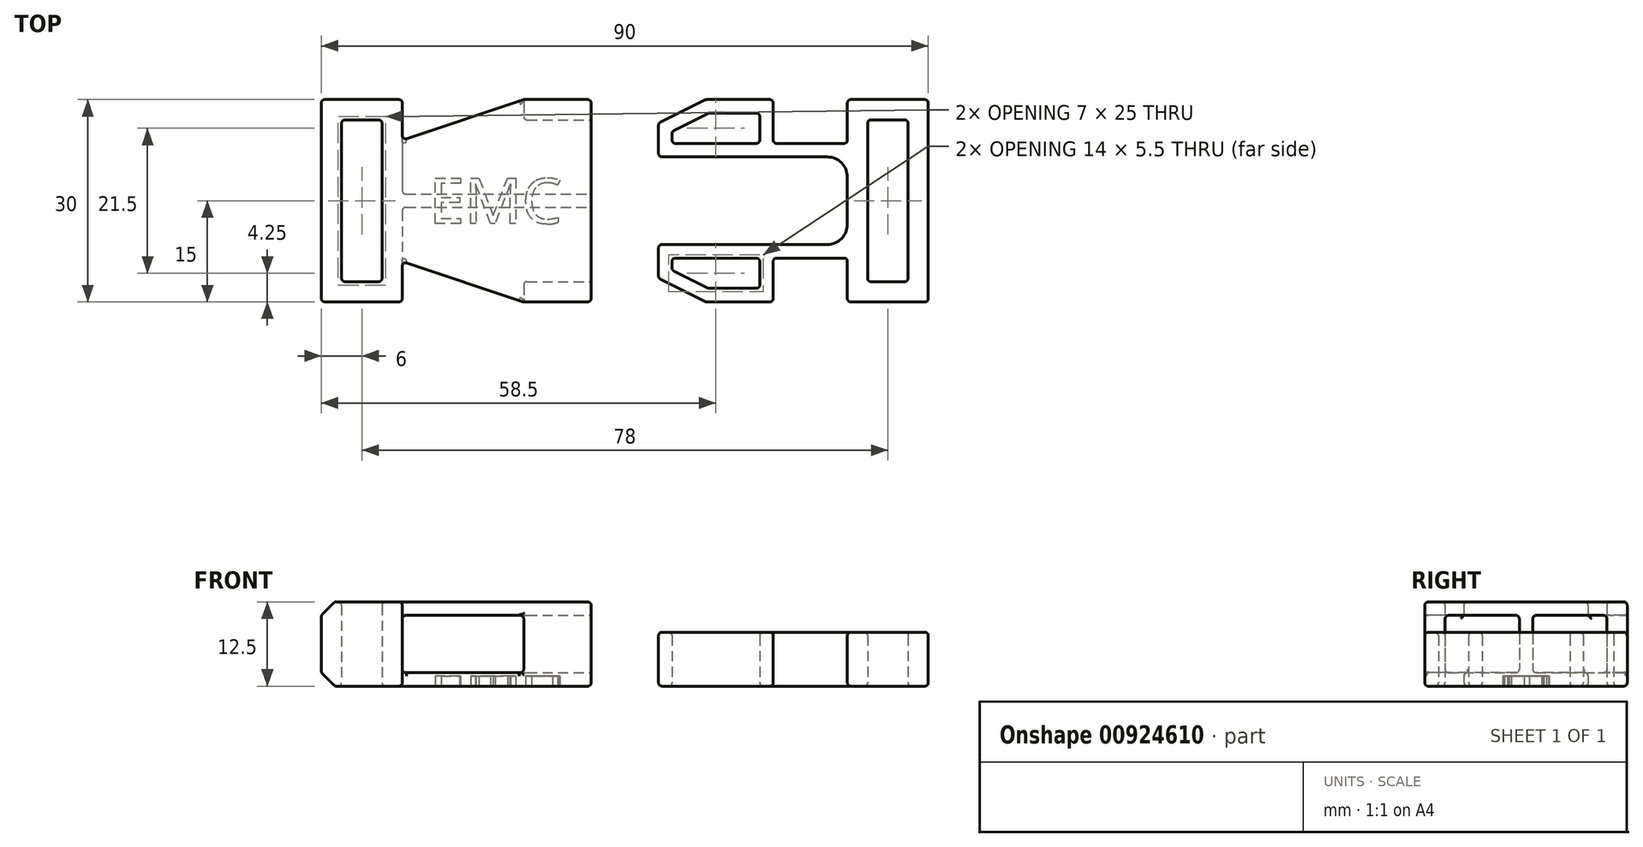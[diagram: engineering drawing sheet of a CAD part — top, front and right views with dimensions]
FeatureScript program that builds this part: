
annotation { "Feature Type Name" : "Feature", "Feature Type Description" : "" }
export const myFeature = defineFeature(function(context is Context, id is Id, definition is map)
    precondition{}
    {
        {
            var Q0;
            Q0=qCreatedBy(makeId("Top.planeOp"),FACE);
            var sketch = newSketch(context, id + "F0", { "sketchPlane" : qUnion([Q0])});
            skLineSegment(sketch, "E0.bottom", {"start": v(-10, 0) * mm, "end": v(-50, 0) * mm, "construction": true});
            skLineSegment(sketch, "E0.top", {"start": v(-10, 30) * mm, "end": v(-50, 30) * mm, "construction": true});
            skLineSegment(sketch, "E0.left", {"start": v(-10, 0) * mm, "end": v(-10, 30) * mm, "construction": true});
            skLineSegment(sketch, "E0.right", {"start": v(-50, 0) * mm, "end": v(-50, 30) * mm, "construction": true});
            skLineSegment(sketch, "E1", {"start": v(-10, 0) * mm, "end": v(-10, 30) * mm});
            skLineSegment(sketch, "E2", {"start": v(-10, 30) * mm, "end": v(-20, 30) * mm});
            skLineSegment(sketch, "E3", {"start": v(-20, 30) * mm, "end": v(-20, 24) * mm});
            skLineSegment(sketch, "E4", {"start": v(-20, 24) * mm, "end": v(-38, 24) * mm});
            skLineSegment(sketch, "E5", {"start": v(-38, 24) * mm, "end": v(-38, 30) * mm});
            skLineSegment(sketch, "E6", {"start": v(-38, 30) * mm, "end": v(-50, 30) * mm});
            skLineSegment(sketch, "E7", {"start": v(-50, 30) * mm, "end": v(-50, 0) * mm});
            skLineSegment(sketch, "E8", {"start": v(-50, 0) * mm, "end": v(-38, 0) * mm});
            skLineSegment(sketch, "E9", {"start": v(-38, 0) * mm, "end": v(-38, 6) * mm});
            skLineSegment(sketch, "E10", {"start": v(-38, 6) * mm, "end": v(-20, 6) * mm});
            skLineSegment(sketch, "E11", {"start": v(-20, 6) * mm, "end": v(-20, 0) * mm});
            skLineSegment(sketch, "E12", {"start": v(-20, 0) * mm, "end": v(-10, 0) * mm});
            skLineSegment(sketch, "E13.bottom", {"start": v(-47, 27) * mm, "end": v(-41, 27) * mm});
            skLineSegment(sketch, "E13.top", {"start": v(-47, 3) * mm, "end": v(-41, 3) * mm});
            skLineSegment(sketch, "E13.left", {"start": v(-47, 27) * mm, "end": v(-47, 3) * mm});
            skLineSegment(sketch, "E13.right", {"start": v(-41, 27) * mm, "end": v(-41, 3) * mm});
            skLineSegment(sketch, "E14.bottom", {"start": v(-38, 16) * mm, "end": v(-10, 16) * mm});
            skLineSegment(sketch, "E14.top", {"start": v(-38, 14) * mm, "end": v(-10, 14) * mm});
            skLineSegment(sketch, "E14.left", {"start": v(-41, 16) * mm, "end": v(-41, 14) * mm});
            skLineSegment(sketch, "E14.right", {"start": v(-10, 16) * mm, "end": v(-10, 14) * mm});
            skLineSegment(sketch, "E15", {"start": v(-20, 27) * mm, "end": v(-10, 27) * mm});
            skLineSegment(sketch, "E16", {"start": v(-20, 3) * mm, "end": v(-10, 3) * mm});
            skLineSegment(sketch, "E17", {"start": v(-50, 15) * mm, "end": v(-10, 15) * mm, "construction": true});
            skLineSegment(sketch, "E18", {"start": v(-10, 30) * mm, "end": v(0, 30) * mm, "construction": true});
            skLineSegment(sketch, "E19", {"start": v(-20, 24) * mm, "end": v(0, 24) * mm, "construction": true});
            skLineSegment(sketch, "E20", {"start": v(-10, 16) * mm, "end": v(0, 16) * mm, "construction": true});
            skLineSegment(sketch, "E21", {"start": v(-10, 15) * mm, "end": v(0, 15) * mm, "construction": true});
            skLineSegment(sketch, "E22", {"start": v(0, 21.5) * mm, "end": v(0, 26.5) * mm});
            skLineSegment(sketch, "E23", {"start": v(0, 26.5) * mm, "end": v(7, 30) * mm});
            skLineSegment(sketch, "E24", {"start": v(7, 30) * mm, "end": v(17, 30) * mm});
            skLineSegment(sketch, "E25", {"start": v(17, 30) * mm, "end": v(17, 23.5) * mm});
            skLineSegment(sketch, "E26", {"start": v(17, 23.5) * mm, "end": v(28, 23.5) * mm});
            skLineSegment(sketch, "E27", {"start": v(28, 23.5) * mm, "end": v(28, 30) * mm});
            skLineSegment(sketch, "E28", {"start": v(28, 30) * mm, "end": v(40, 30) * mm});
            skLineSegment(sketch, "E29", {"start": v(40, 30) * mm, "end": v(40, 15) * mm});
            skLineSegment(sketch, "E30", {"start": v(28, 15) * mm, "end": v(28, 18.5) * mm});
            skLineSegment(sketch, "E31", {"start": v(25, 21.5) * mm, "end": v(0, 21.5) * mm});
            skLineSegment(sketch, "E32.MirrorCS", {"start": v(25, 8.5) * mm, "end": v(0, 8.5) * mm});
            skLineSegment(sketch, "E33.MirrorCS", {"start": v(28, 15) * mm, "end": v(28, 11.5) * mm});
            skLineSegment(sketch, "E34.MirrorCS", {"start": v(40, 0) * mm, "end": v(40, 15) * mm});
            skLineSegment(sketch, "E35.MirrorCS", {"start": v(28, 0) * mm, "end": v(40, 0) * mm});
            skLineSegment(sketch, "E36.MirrorCS", {"start": v(28, 6.5) * mm, "end": v(28, 0) * mm});
            skLineSegment(sketch, "E37.MirrorCS", {"start": v(17, 6.5) * mm, "end": v(28, 6.5) * mm});
            skLineSegment(sketch, "E38.MirrorCS", {"start": v(17, 0) * mm, "end": v(17, 6.5) * mm});
            skLineSegment(sketch, "E39.MirrorCS", {"start": v(7, 0) * mm, "end": v(17, 0) * mm});
            skLineSegment(sketch, "E40.MirrorCS", {"start": v(0, 3.5) * mm, "end": v(7, 0) * mm});
            skLineSegment(sketch, "E41.MirrorCS", {"start": v(0, 8.5) * mm, "end": v(0, 3.5) * mm});
            skPoint(sketch, "E42.visualSharp", {"position": v(28, 21.5) * mm});
            skArc(sketch, "E42.filletArc", {"start": v(28, 18.5) * mm, "mid": v(27.12, 20.62) * mm, "end": v(25, 21.5) * mm});
            skPoint(sketch, "E43.visualSharp", {"position": v(28, 8.5) * mm});
            skArc(sketch, "E43.filletArc", {"start": v(25, 8.5) * mm, "mid": v(27.12, 9.38) * mm, "end": v(28, 11.5) * mm});
            skLineSegment(sketch, "E44.bottom", {"start": v(31, 27) * mm, "end": v(37, 27) * mm});
            skLineSegment(sketch, "E44.top", {"start": v(31, 3) * mm, "end": v(37, 3) * mm});
            skLineSegment(sketch, "E44.left", {"start": v(31, 27) * mm, "end": v(31, 3) * mm});
            skLineSegment(sketch, "E44.right", {"start": v(37, 27) * mm, "end": v(37, 3) * mm});
            skLineSegment(sketch, "E45.0", {"start": v(15, 28) * mm, "end": v(15, 23.5) * mm});
            skLineSegment(sketch, "E45.1", {"start": v(7.47, 28) * mm, "end": v(15, 28) * mm});
            skLineSegment(sketch, "E45.2", {"start": v(2, 25.26) * mm, "end": v(7.47, 28) * mm});
            skLineSegment(sketch, "E45.3", {"start": v(2, 23.5) * mm, "end": v(2, 25.26) * mm});
            skLineSegment(sketch, "E46", {"start": v(2, 23.5) * mm, "end": v(15, 23.5) * mm});
            skLineSegment(sketch, "E47.MirrorCS", {"start": v(2, 6.5) * mm, "end": v(15, 6.5) * mm});
            skLineSegment(sketch, "E48.MirrorCS", {"start": v(2, 6.5) * mm, "end": v(2, 4.74) * mm});
            skLineSegment(sketch, "E49.MirrorCS", {"start": v(2, 4.74) * mm, "end": v(7.47, 2) * mm});
            skLineSegment(sketch, "E50.MirrorCS", {"start": v(7.47, 2) * mm, "end": v(15, 2) * mm});
            skLineSegment(sketch, "E51.MirrorCS", {"start": v(15, 2) * mm, "end": v(15, 6.5) * mm});
            skLineSegment(sketch, "E52", {"start": v(-38, 24) * mm, "end": v(-38, 6) * mm});
            skLineSegment(sketch, "E53", {"start": v(-38, 6) * mm, "end": v(-20, 0) * mm});
            skLineSegment(sketch, "E54", {"start": v(-38, 24) * mm, "end": v(-20, 30) * mm});
            skSolve(sketch);
        }
        {
            var Q0;
            Q0=makeQuery(id+"F0.imprint","IMPRINT",FACE,{"disambiguationData":[TD([[makeQuery(id+"F0.imprint","IMPRINT",EDGE,{"derivedFrom":sQuery(id+"F0.wireOp",EDGE,"E22")}),-1.0]])]});
            extrude(context, id + "F1", {"entities" : qUnion([Q0]), "depth" : 8 * mm, "offsetDistance" : 25 * mm});
        }
        {
            var Q0;
            {var subQ1=sQuery(id+"F0.wireOp",EDGE,"E4");Q0=makeQuery(id+"F0.imprint","IMPRINT",FACE,{"disambiguationData":[TD([[makeQuery(id+"F0.imprint","IMPRINT",EDGE,{"derivedFrom":subQ1}),1.0]])]});}
            var Q1;
            {var subQ1=sQuery(id+"F0.wireOp",EDGE,"E10");Q1=makeQuery(id+"F0.imprint","IMPRINT",FACE,{"disambiguationData":[TD([[makeQuery(id+"F0.imprint","IMPRINT",EDGE,{"derivedFrom":subQ1}),1.0]])]});}
            var Q2;
            {var subQ0=sQuery(id+"F0.wireOp",EDGE,"E12");Q2=makeQuery(id+"F0.imprint","IMPRINT",FACE,{"disambiguationData":[TD([[makeQuery(id+"F0.imprint","IMPRINT",EDGE,{"derivedFrom":subQ0}),1.0]])]});}
            var Q3;
            {var subQ2=sQuery(id+"F0.wireOp",EDGE,"E5");Q3=makeQuery(id+"F0.imprint","IMPRINT",FACE,{"disambiguationData":[TD([[makeQuery(id+"F0.imprint","IMPRINT",EDGE,{"derivedFrom":subQ2}),1.0]])]});}
            var Q4;
            {var subQ0=sQuery(id+"F0.wireOp",EDGE,"E2");Q4=makeQuery(id+"F0.imprint","IMPRINT",FACE,{"disambiguationData":[TD([[makeQuery(id+"F0.imprint","IMPRINT",EDGE,{"derivedFrom":subQ0}),1.0]])]});}
            var Q5;
            {var subQ0=sQuery(id+"F0.wireOp",EDGE,"E14.bottom");Q5=makeQuery(id+"F0.imprint","IMPRINT",FACE,{"disambiguationData":[TD([[makeQuery(id+"F0.imprint","IMPRINT",EDGE,{"derivedFrom":subQ0}),-1.0]])]});}
            var Q6;
            {var subQ0=sQuery(id+"F0.wireOp",EDGE,"E10");Q6=makeQuery(id+"F0.imprint","IMPRINT",FACE,{"disambiguationData":[TD([[makeQuery(id+"F0.imprint","IMPRINT",EDGE,{"derivedFrom":subQ0}),-1.0]])]});}
            var Q7;
            {var subQ2=sQuery(id+"F0.wireOp",EDGE,"E4");Q7=makeQuery(id+"F0.imprint","IMPRINT",FACE,{"disambiguationData":[TD([[makeQuery(id+"F0.imprint","IMPRINT",EDGE,{"derivedFrom":subQ2}),-1.0]])]});}
            extrude(context, id + "F2", {"entities" : qUnion([Q0, Q1, Q2, Q3, Q4, Q5, Q6, Q7]), "depth" : (8.5 + 4) * mm, "offsetDistance" : 25 * mm});
        }
        {
            var Q0;
            {var subQ1=sQuery(id+"F0.wireOp",EDGE,"E10");Q0=makeQuery(id+"F0.imprint","IMPRINT",FACE,{"disambiguationData":[TD([[makeQuery(id+"F0.imprint","IMPRINT",EDGE,{"derivedFrom":subQ1}),1.0]])]});}
            var Q1;
            {var subQ1=sQuery(id+"F0.wireOp",EDGE,"E4");Q1=makeQuery(id+"F0.imprint","IMPRINT",FACE,{"disambiguationData":[TD([[makeQuery(id+"F0.imprint","IMPRINT",EDGE,{"derivedFrom":subQ1}),1.0]])]});}
            var Q2;
            {var subQ0=sQuery(id+"F0.wireOp",EDGE,"E10");Q2=makeQuery(id+"F0.imprint","IMPRINT",FACE,{"disambiguationData":[TD([[makeQuery(id+"F0.imprint","IMPRINT",EDGE,{"derivedFrom":subQ0}),-1.0]])]});}
            var Q3;
            {var subQ2=sQuery(id+"F0.wireOp",EDGE,"E4");Q3=makeQuery(id+"F0.imprint","IMPRINT",FACE,{"disambiguationData":[TD([[makeQuery(id+"F0.imprint","IMPRINT",EDGE,{"derivedFrom":subQ2}),-1.0]])]});}
            extrude(context, id + "F3", {"entities" : qUnion([Q0, Q1, Q2, Q3]), "operationType" : NewBodyOperationType.REMOVE, "depth" : (8.5 + 2) * mm, "offsetDistance" : 25 * mm, "hasSecondDirection" : true, "secondDirectionOppositeDirection" : false, "secondDirectionDepth" : 2 * mm});
        }
        {
            var Q0;
            Q0=makeQuery(id+"F2.opExtrude","CAP_EDGE",EDGE,{"disambiguationData":[OSD([sQuery(id+"F0.wireOp",EDGE,"E7")])],"isStart":false});
            var Q1;
            Q1=makeQuery(id+"F2.opExtrude","CAP_EDGE",EDGE,{"disambiguationData":[OSD([sQuery(id+"F0.wireOp",EDGE,"E7")])],"isStart":true});
            chamfer(context, id + "F4", {"entities" : qUnion([Q0, Q1]), "width" : 2 * mm, "tangentPropagation" : true});
        }
        {
            var Q0;
            Q0=makeQuery(id+"F1.opExtrude","CAP_FACE",FACE,{"disambiguationData":[OSD([sQuery(id+"F0.wireOp",EDGE,"E22"),sQuery(id+"F0.wireOp",EDGE,"E23"),sQuery(id+"F0.wireOp",EDGE,"E24"),sQuery(id+"F0.wireOp",EDGE,"E25"),sQuery(id+"F0.wireOp",EDGE,"E26"),sQuery(id+"F0.wireOp",EDGE,"E27"),sQuery(id+"F0.wireOp",EDGE,"E28"),sQuery(id+"F0.wireOp",EDGE,"E29"),sQuery(id+"F0.wireOp",EDGE,"E30"),sQuery(id+"F0.wireOp",EDGE,"E31"),sQuery(id+"F0.wireOp",EDGE,"E32.MirrorCS"),sQuery(id+"F0.wireOp",EDGE,"E33.MirrorCS"),sQuery(id+"F0.wireOp",EDGE,"E34.MirrorCS"),sQuery(id+"F0.wireOp",EDGE,"E35.MirrorCS"),sQuery(id+"F0.wireOp",EDGE,"E36.MirrorCS"),sQuery(id+"F0.wireOp",EDGE,"E37.MirrorCS"),sQuery(id+"F0.wireOp",EDGE,"E38.MirrorCS"),sQuery(id+"F0.wireOp",EDGE,"E39.MirrorCS"),sQuery(id+"F0.wireOp",EDGE,"E40.MirrorCS"),sQuery(id+"F0.wireOp",EDGE,"E41.MirrorCS"),sQuery(id+"F0.wireOp",EDGE,"E42.filletArc"),sQuery(id+"F0.wireOp",EDGE,"E43.filletArc"),sQuery(id+"F0.wireOp",EDGE,"E44.bottom"),sQuery(id+"F0.wireOp",EDGE,"E44.top"),sQuery(id+"F0.wireOp",EDGE,"E44.left"),sQuery(id+"F0.wireOp",EDGE,"E44.right"),sQuery(id+"F0.wireOp",EDGE,"E45.0"),sQuery(id+"F0.wireOp",EDGE,"E45.1"),sQuery(id+"F0.wireOp",EDGE,"E45.2"),sQuery(id+"F0.wireOp",EDGE,"E45.3"),sQuery(id+"F0.wireOp",EDGE,"E46"),sQuery(id+"F0.wireOp",EDGE,"E47.MirrorCS"),sQuery(id+"F0.wireOp",EDGE,"E48.MirrorCS"),sQuery(id+"F0.wireOp",EDGE,"E49.MirrorCS"),sQuery(id+"F0.wireOp",EDGE,"E50.MirrorCS"),sQuery(id+"F0.wireOp",EDGE,"E51.MirrorCS")])],"isStart":false});
            var Q1;
            Q1=makeQuery(id+"F1.opExtrude","CAP_FACE",FACE,{"disambiguationData":[OSD([sQuery(id+"F0.wireOp",EDGE,"E22"),sQuery(id+"F0.wireOp",EDGE,"E23"),sQuery(id+"F0.wireOp",EDGE,"E24"),sQuery(id+"F0.wireOp",EDGE,"E25"),sQuery(id+"F0.wireOp",EDGE,"E26"),sQuery(id+"F0.wireOp",EDGE,"E27"),sQuery(id+"F0.wireOp",EDGE,"E28"),sQuery(id+"F0.wireOp",EDGE,"E29"),sQuery(id+"F0.wireOp",EDGE,"E30"),sQuery(id+"F0.wireOp",EDGE,"E31"),sQuery(id+"F0.wireOp",EDGE,"E32.MirrorCS"),sQuery(id+"F0.wireOp",EDGE,"E33.MirrorCS"),sQuery(id+"F0.wireOp",EDGE,"E34.MirrorCS"),sQuery(id+"F0.wireOp",EDGE,"E35.MirrorCS"),sQuery(id+"F0.wireOp",EDGE,"E36.MirrorCS"),sQuery(id+"F0.wireOp",EDGE,"E37.MirrorCS"),sQuery(id+"F0.wireOp",EDGE,"E38.MirrorCS"),sQuery(id+"F0.wireOp",EDGE,"E39.MirrorCS"),sQuery(id+"F0.wireOp",EDGE,"E40.MirrorCS"),sQuery(id+"F0.wireOp",EDGE,"E41.MirrorCS"),sQuery(id+"F0.wireOp",EDGE,"E42.filletArc"),sQuery(id+"F0.wireOp",EDGE,"E43.filletArc"),sQuery(id+"F0.wireOp",EDGE,"E44.bottom"),sQuery(id+"F0.wireOp",EDGE,"E44.top"),sQuery(id+"F0.wireOp",EDGE,"E44.left"),sQuery(id+"F0.wireOp",EDGE,"E44.right"),sQuery(id+"F0.wireOp",EDGE,"E45.0"),sQuery(id+"F0.wireOp",EDGE,"E45.1"),sQuery(id+"F0.wireOp",EDGE,"E45.2"),sQuery(id+"F0.wireOp",EDGE,"E45.3"),sQuery(id+"F0.wireOp",EDGE,"E46"),sQuery(id+"F0.wireOp",EDGE,"E47.MirrorCS"),sQuery(id+"F0.wireOp",EDGE,"E48.MirrorCS"),sQuery(id+"F0.wireOp",EDGE,"E49.MirrorCS"),sQuery(id+"F0.wireOp",EDGE,"E50.MirrorCS"),sQuery(id+"F0.wireOp",EDGE,"E51.MirrorCS")])],"isStart":true});
            var Q2;
            Q2=makeQuery(id+"F1.opExtrude","CAP_EDGE",EDGE,{"disambiguationData":[OSD([sQuery(id+"F0.wireOp",EDGE,"E29"),sQuery(id+"F0.wireOp",EDGE,"E34.MirrorCS")])],"isStart":false});
            var Q3;
            Q3=makeQuery(id+"F1.opExtrude","CAP_EDGE",EDGE,{"disambiguationData":[OSD([sQuery(id+"F0.wireOp",EDGE,"E29"),sQuery(id+"F0.wireOp",EDGE,"E34.MirrorCS")])],"isStart":true});
            var Q4;
            Q4=makeQuery(id+"F1.opExtrude","SWEPT_EDGE",EDGE,{"disambiguationData":[OSD([sQuery(id+"F0.wireOp",EDGE,"E28"),sQuery(id+"F0.wireOp",EDGE,"E29")])]});
            var Q5;
            Q5=makeQuery(id+"F1.opExtrude","SWEPT_EDGE",EDGE,{"disambiguationData":[OSD([sQuery(id+"F0.wireOp",EDGE,"E34.MirrorCS"),sQuery(id+"F0.wireOp",EDGE,"E35.MirrorCS")])]});
            var Q6;
            Q6=makeQuery(id+"F1.opExtrude","SWEPT_EDGE",EDGE,{"disambiguationData":[OSD([sQuery(id+"F0.wireOp",EDGE,"E39.MirrorCS"),sQuery(id+"F0.wireOp",EDGE,"E40.MirrorCS")])]});
            var Q7;
            Q7=makeQuery(id+"F1.opExtrude","SWEPT_EDGE",EDGE,{"disambiguationData":[OSD([sQuery(id+"F0.wireOp",EDGE,"E38.MirrorCS"),sQuery(id+"F0.wireOp",EDGE,"E39.MirrorCS")])]});
            var Q8;
            Q8=makeQuery(id+"F1.opExtrude","SWEPT_EDGE",EDGE,{"disambiguationData":[OSD([sQuery(id+"F0.wireOp",EDGE,"E44.bottom"),sQuery(id+"F0.wireOp",EDGE,"E44.left")])]});
            var Q9;
            Q9=makeQuery(id+"F1.opExtrude","CAP_EDGE",EDGE,{"disambiguationData":[OSD([sQuery(id+"F0.wireOp",EDGE,"E44.left")])],"isStart":false});
            var Q10;
            Q10=makeQuery(id+"F1.opExtrude","SWEPT_EDGE",EDGE,{"disambiguationData":[OSD([sQuery(id+"F0.wireOp",EDGE,"E40.MirrorCS"),sQuery(id+"F0.wireOp",EDGE,"E41.MirrorCS")])]});
            var Q11;
            Q11=makeQuery(id+"F1.opExtrude","SWEPT_EDGE",EDGE,{"disambiguationData":[OSD([sQuery(id+"F0.wireOp",EDGE,"E37.MirrorCS"),sQuery(id+"F0.wireOp",EDGE,"E38.MirrorCS")])]});
            var Q12;
            Q12=makeQuery(id+"F1.opExtrude","SWEPT_EDGE",EDGE,{"disambiguationData":[OSD([sQuery(id+"F0.wireOp",EDGE,"E35.MirrorCS"),sQuery(id+"F0.wireOp",EDGE,"E36.MirrorCS")])]});
            var Q13;
            Q13=makeQuery(id+"F1.opExtrude","CAP_EDGE",EDGE,{"disambiguationData":[OSD([sQuery(id+"F0.wireOp",EDGE,"E44.bottom")])],"isStart":false});
            var Q14;
            Q14=makeQuery(id+"F1.opExtrude","CAP_EDGE",EDGE,{"disambiguationData":[OSD([sQuery(id+"F0.wireOp",EDGE,"E39.MirrorCS")])],"isStart":true});
            var Q15;
            Q15=makeQuery(id+"F1.opExtrude","CAP_EDGE",EDGE,{"disambiguationData":[OSD([sQuery(id+"F0.wireOp",EDGE,"E38.MirrorCS")])],"isStart":false});
            var Q16;
            Q16=makeQuery(id+"F1.opExtrude","CAP_EDGE",EDGE,{"disambiguationData":[OSD([sQuery(id+"F0.wireOp",EDGE,"E40.MirrorCS")])],"isStart":true});
            var Q17;
            Q17=makeQuery(id+"F1.opExtrude","SWEPT_EDGE",EDGE,{"disambiguationData":[OSD([sQuery(id+"F0.wireOp",EDGE,"E44.bottom"),sQuery(id+"F0.wireOp",EDGE,"E44.right")])]});
            var Q18;
            Q18=makeQuery(id+"F1.opExtrude","SWEPT_EDGE",EDGE,{"disambiguationData":[OSD([sQuery(id+"F0.wireOp",EDGE,"E22"),sQuery(id+"F0.wireOp",EDGE,"E31")])]});
            var Q19;
            Q19=makeQuery(id+"F1.opExtrude","SWEPT_EDGE",EDGE,{"disambiguationData":[OSD([sQuery(id+"F0.wireOp",EDGE,"E45.3"),sQuery(id+"F0.wireOp",EDGE,"E46")])]});
            var Q20;
            Q20=makeQuery(id+"F1.opExtrude","SWEPT_EDGE",EDGE,{"disambiguationData":[OSD([sQuery(id+"F0.wireOp",EDGE,"E45.1"),sQuery(id+"F0.wireOp",EDGE,"E45.2")])]});
            var Q21;
            Q21=makeQuery(id+"F1.opExtrude","CAP_EDGE",EDGE,{"disambiguationData":[OSD([sQuery(id+"F0.wireOp",EDGE,"E45.1")])],"isStart":false});
            var Q22;
            Q22=makeQuery(id+"F1.opExtrude","CAP_EDGE",EDGE,{"disambiguationData":[OSD([sQuery(id+"F0.wireOp",EDGE,"E43.filletArc")])],"isStart":false});
            var Q23;
            Q23=makeQuery(id+"F1.opExtrude","CAP_EDGE",EDGE,{"disambiguationData":[OSD([sQuery(id+"F0.wireOp",EDGE,"E46")])],"isStart":false});
            var Q24;
            Q24=makeQuery(id+"F1.opExtrude","SWEPT_EDGE",EDGE,{"disambiguationData":[OSD([sQuery(id+"F0.wireOp",EDGE,"E26"),sQuery(id+"F0.wireOp",EDGE,"E27")])]});
            var Q25;
            Q25=makeQuery(id+"F1.opExtrude","CAP_EDGE",EDGE,{"disambiguationData":[OSD([sQuery(id+"F0.wireOp",EDGE,"E47.MirrorCS")])],"isStart":false});
            var Q26;
            Q26=makeQuery(id+"F1.opExtrude","SWEPT_EDGE",EDGE,{"disambiguationData":[OSD([sQuery(id+"F0.wireOp",EDGE,"E45.0"),sQuery(id+"F0.wireOp",EDGE,"E46")])]});
            var Q27;
            Q27=makeQuery(id+"F1.opExtrude","CAP_EDGE",EDGE,{"disambiguationData":[OSD([sQuery(id+"F0.wireOp",EDGE,"E44.right")])],"isStart":true});
            var Q28;
            Q28=makeQuery(id+"F1.opExtrude","SWEPT_EDGE",EDGE,{"disambiguationData":[OSD([sQuery(id+"F0.wireOp",EDGE,"E44.top"),sQuery(id+"F0.wireOp",EDGE,"E44.left")])]});
            var Q29;
            Q29=makeQuery(id+"F1.opExtrude","SWEPT_EDGE",EDGE,{"disambiguationData":[OSD([sQuery(id+"F0.wireOp",EDGE,"E47.MirrorCS"),sQuery(id+"F0.wireOp",EDGE,"E51.MirrorCS")])]});
            var Q30;
            Q30=makeQuery(id+"F1.opExtrude","CAP_EDGE",EDGE,{"disambiguationData":[OSD([sQuery(id+"F0.wireOp",EDGE,"E41.MirrorCS")])],"isStart":true});
            var Q31;
            Q31=makeQuery(id+"F1.opExtrude","CAP_EDGE",EDGE,{"disambiguationData":[OSD([sQuery(id+"F0.wireOp",EDGE,"E38.MirrorCS")])],"isStart":true});
            var Q32;
            Q32=makeQuery(id+"F1.opExtrude","CAP_EDGE",EDGE,{"disambiguationData":[OSD([sQuery(id+"F0.wireOp",EDGE,"E31")])],"isStart":false});
            var Q33;
            Q33=makeQuery(id+"F1.opExtrude","CAP_EDGE",EDGE,{"disambiguationData":[OSD([sQuery(id+"F0.wireOp",EDGE,"E37.MirrorCS")])],"isStart":true});
            var Q34;
            Q34=makeQuery(id+"F1.opExtrude","CAP_EDGE",EDGE,{"disambiguationData":[OSD([sQuery(id+"F0.wireOp",EDGE,"E48.MirrorCS")])],"isStart":false});
            var Q35;
            Q35=makeQuery(id+"F1.opExtrude","SWEPT_EDGE",EDGE,{"disambiguationData":[OSD([sQuery(id+"F0.wireOp",EDGE,"E47.MirrorCS"),sQuery(id+"F0.wireOp",EDGE,"E48.MirrorCS")])]});
            var Q36;
            Q36=makeQuery(id+"F1.opExtrude","CAP_EDGE",EDGE,{"disambiguationData":[OSD([sQuery(id+"F0.wireOp",EDGE,"E35.MirrorCS")])],"isStart":true});
            var Q37;
            Q37=makeQuery(id+"F1.opExtrude","CAP_EDGE",EDGE,{"disambiguationData":[OSD([sQuery(id+"F0.wireOp",EDGE,"E30"),sQuery(id+"F0.wireOp",EDGE,"E33.MirrorCS")])],"isStart":false});
            var Q38;
            Q38=makeQuery(id+"F1.opExtrude","CAP_EDGE",EDGE,{"disambiguationData":[OSD([sQuery(id+"F0.wireOp",EDGE,"E42.filletArc")])],"isStart":false});
            var Q39;
            Q39=makeQuery(id+"F1.opExtrude","SWEPT_EDGE",EDGE,{"disambiguationData":[OSD([sQuery(id+"F0.wireOp",EDGE,"E44.top"),sQuery(id+"F0.wireOp",EDGE,"E44.right")])]});
            var Q40;
            Q40=makeQuery(id+"F1.opExtrude","SWEPT_EDGE",EDGE,{"disambiguationData":[OSD([sQuery(id+"F0.wireOp",EDGE,"E32.MirrorCS"),sQuery(id+"F0.wireOp",EDGE,"E41.MirrorCS")])]});
            var Q41;
            Q41=makeQuery(id+"F1.opExtrude","CAP_EDGE",EDGE,{"disambiguationData":[OSD([sQuery(id+"F0.wireOp",EDGE,"E40.MirrorCS")])],"isStart":false});
            var Q42;
            Q42=makeQuery(id+"F1.opExtrude","SWEPT_EDGE",EDGE,{"disambiguationData":[OSD([sQuery(id+"F0.wireOp",EDGE,"E49.MirrorCS"),sQuery(id+"F0.wireOp",EDGE,"E50.MirrorCS")])]});
            var Q43;
            Q43=makeQuery(id+"F1.opExtrude","CAP_EDGE",EDGE,{"disambiguationData":[OSD([sQuery(id+"F0.wireOp",EDGE,"E36.MirrorCS")])],"isStart":false});
            var Q44;
            Q44=makeQuery(id+"F1.opExtrude","CAP_EDGE",EDGE,{"disambiguationData":[OSD([sQuery(id+"F0.wireOp",EDGE,"E28")])],"isStart":true});
            var Q45;
            Q45=makeQuery(id+"F1.opExtrude","CAP_EDGE",EDGE,{"disambiguationData":[OSD([sQuery(id+"F0.wireOp",EDGE,"E37.MirrorCS")])],"isStart":false});
            var Q46;
            Q46=makeQuery(id+"F1.opExtrude","CAP_EDGE",EDGE,{"disambiguationData":[OSD([sQuery(id+"F0.wireOp",EDGE,"E28")])],"isStart":false});
            var Q47;
            Q47=makeQuery(id+"F1.opExtrude","SWEPT_EDGE",EDGE,{"disambiguationData":[OSD([sQuery(id+"F0.wireOp",EDGE,"E27"),sQuery(id+"F0.wireOp",EDGE,"E28")])]});
            var Q48;
            Q48=makeQuery(id+"F1.opExtrude","CAP_EDGE",EDGE,{"disambiguationData":[OSD([sQuery(id+"F0.wireOp",EDGE,"E39.MirrorCS")])],"isStart":false});
            var Q49;
            Q49=makeQuery(id+"F1.opExtrude","CAP_EDGE",EDGE,{"disambiguationData":[OSD([sQuery(id+"F0.wireOp",EDGE,"E44.bottom")])],"isStart":true});
            var Q50;
            Q50=makeQuery(id+"F1.opExtrude","CAP_EDGE",EDGE,{"disambiguationData":[OSD([sQuery(id+"F0.wireOp",EDGE,"E44.right")])],"isStart":false});
            var Q51;
            Q51=makeQuery(id+"F1.opExtrude","SWEPT_EDGE",EDGE,{"disambiguationData":[OSD([sQuery(id+"F0.wireOp",EDGE,"E50.MirrorCS"),sQuery(id+"F0.wireOp",EDGE,"E51.MirrorCS")])]});
            var Q52;
            Q52=makeQuery(id+"F1.opExtrude","CAP_EDGE",EDGE,{"disambiguationData":[OSD([sQuery(id+"F0.wireOp",EDGE,"E45.0")])],"isStart":false});
            var Q53;
            Q53=makeQuery(id+"F1.opExtrude","CAP_EDGE",EDGE,{"disambiguationData":[OSD([sQuery(id+"F0.wireOp",EDGE,"E35.MirrorCS")])],"isStart":false});
            var Q54;
            Q54=makeQuery(id+"F1.opExtrude","CAP_EDGE",EDGE,{"disambiguationData":[OSD([sQuery(id+"F0.wireOp",EDGE,"E45.2")])],"isStart":false});
            var Q55;
            Q55=makeQuery(id+"F1.opExtrude","CAP_EDGE",EDGE,{"disambiguationData":[OSD([sQuery(id+"F0.wireOp",EDGE,"E49.MirrorCS")])],"isStart":true});
            var Q56;
            Q56=makeQuery(id+"F1.opExtrude","SWEPT_EDGE",EDGE,{"disambiguationData":[OSD([sQuery(id+"F0.wireOp",EDGE,"E36.MirrorCS"),sQuery(id+"F0.wireOp",EDGE,"E37.MirrorCS")])]});
            var Q57;
            Q57=makeQuery(id+"F1.opExtrude","SWEPT_EDGE",EDGE,{"disambiguationData":[OSD([sQuery(id+"F0.wireOp",EDGE,"E25"),sQuery(id+"F0.wireOp",EDGE,"E26")])]});
            var Q58;
            Q58=makeQuery(id+"F1.opExtrude","SWEPT_EDGE",EDGE,{"disambiguationData":[OSD([sQuery(id+"F0.wireOp",EDGE,"E48.MirrorCS"),sQuery(id+"F0.wireOp",EDGE,"E49.MirrorCS")])]});
            var Q59;
            Q59=makeQuery(id+"F1.opExtrude","CAP_EDGE",EDGE,{"disambiguationData":[OSD([sQuery(id+"F0.wireOp",EDGE,"E44.left")])],"isStart":true});
            var Q60;
            Q60=makeQuery(id+"F1.opExtrude","SWEPT_EDGE",EDGE,{"disambiguationData":[OSD([sQuery(id+"F0.wireOp",EDGE,"E32.MirrorCS"),sQuery(id+"F0.wireOp",EDGE,"E43.filletArc")])]});
            var Q61;
            Q61=makeQuery(id+"F1.opExtrude","CAP_EDGE",EDGE,{"disambiguationData":[OSD([sQuery(id+"F0.wireOp",EDGE,"E45.2")])],"isStart":true});
            var Q62;
            Q62=makeQuery(id+"F1.opExtrude","CAP_EDGE",EDGE,{"disambiguationData":[OSD([sQuery(id+"F0.wireOp",EDGE,"E49.MirrorCS")])],"isStart":false});
            var Q63;
            Q63=makeQuery(id+"F1.opExtrude","CAP_EDGE",EDGE,{"disambiguationData":[OSD([sQuery(id+"F0.wireOp",EDGE,"E26")])],"isStart":false});
            var Q64;
            Q64=makeQuery(id+"F1.opExtrude","CAP_EDGE",EDGE,{"disambiguationData":[OSD([sQuery(id+"F0.wireOp",EDGE,"E22")])],"isStart":false});
            var Q65;
            Q65=makeQuery(id+"F1.opExtrude","CAP_EDGE",EDGE,{"disambiguationData":[OSD([sQuery(id+"F0.wireOp",EDGE,"E50.MirrorCS")])],"isStart":true});
            var Q66;
            Q66=makeQuery(id+"F1.opExtrude","CAP_EDGE",EDGE,{"disambiguationData":[OSD([sQuery(id+"F0.wireOp",EDGE,"E25")])],"isStart":false});
            var Q67;
            Q67=makeQuery(id+"F1.opExtrude","SWEPT_EDGE",EDGE,{"disambiguationData":[OSD([sQuery(id+"F0.wireOp",EDGE,"E45.0"),sQuery(id+"F0.wireOp",EDGE,"E45.1")])]});
            var Q68;
            Q68=makeQuery(id+"F1.opExtrude","CAP_EDGE",EDGE,{"disambiguationData":[OSD([sQuery(id+"F0.wireOp",EDGE,"E26")])],"isStart":true});
            var Q69;
            Q69=makeQuery(id+"F1.opExtrude","CAP_EDGE",EDGE,{"disambiguationData":[OSD([sQuery(id+"F0.wireOp",EDGE,"E24")])],"isStart":false});
            var Q70;
            Q70=makeQuery(id+"F1.opExtrude","SWEPT_EDGE",EDGE,{"disambiguationData":[OSD([sQuery(id+"F0.wireOp",EDGE,"E31"),sQuery(id+"F0.wireOp",EDGE,"E42.filletArc")])]});
            var Q71;
            Q71=makeQuery(id+"F1.opExtrude","CAP_EDGE",EDGE,{"disambiguationData":[OSD([sQuery(id+"F0.wireOp",EDGE,"E51.MirrorCS")])],"isStart":false});
            var Q72;
            Q72=makeQuery(id+"F1.opExtrude","CAP_EDGE",EDGE,{"disambiguationData":[OSD([sQuery(id+"F0.wireOp",EDGE,"E45.1")])],"isStart":true});
            var Q73;
            Q73=makeQuery(id+"F1.opExtrude","SWEPT_EDGE",EDGE,{"disambiguationData":[OSD([sQuery(id+"F0.wireOp",EDGE,"E30"),sQuery(id+"F0.wireOp",EDGE,"E42.filletArc")])]});
            var Q74;
            Q74=makeQuery(id+"F1.opExtrude","CAP_EDGE",EDGE,{"disambiguationData":[OSD([sQuery(id+"F0.wireOp",EDGE,"E42.filletArc")])],"isStart":true});
            var Q75;
            Q75=makeQuery(id+"F1.opExtrude","CAP_EDGE",EDGE,{"disambiguationData":[OSD([sQuery(id+"F0.wireOp",EDGE,"E41.MirrorCS")])],"isStart":false});
            var Q76;
            Q76=makeQuery(id+"F1.opExtrude","CAP_EDGE",EDGE,{"disambiguationData":[OSD([sQuery(id+"F0.wireOp",EDGE,"E36.MirrorCS")])],"isStart":true});
            var Q77;
            Q77=makeQuery(id+"F1.opExtrude","CAP_EDGE",EDGE,{"disambiguationData":[OSD([sQuery(id+"F0.wireOp",EDGE,"E27")])],"isStart":false});
            var Q78;
            Q78=makeQuery(id+"F1.opExtrude","CAP_EDGE",EDGE,{"disambiguationData":[OSD([sQuery(id+"F0.wireOp",EDGE,"E24")])],"isStart":true});
            var Q79;
            Q79=makeQuery(id+"F1.opExtrude","CAP_EDGE",EDGE,{"disambiguationData":[OSD([sQuery(id+"F0.wireOp",EDGE,"E44.top")])],"isStart":true});
            var Q80;
            Q80=makeQuery(id+"F1.opExtrude","SWEPT_EDGE",EDGE,{"disambiguationData":[OSD([sQuery(id+"F0.wireOp",EDGE,"E33.MirrorCS"),sQuery(id+"F0.wireOp",EDGE,"E43.filletArc")])]});
            var Q81;
            Q81=makeQuery(id+"F1.opExtrude","SWEPT_EDGE",EDGE,{"disambiguationData":[OSD([sQuery(id+"F0.wireOp",EDGE,"E23"),sQuery(id+"F0.wireOp",EDGE,"E24")])]});
            var Q82;
            Q82=makeQuery(id+"F1.opExtrude","SWEPT_EDGE",EDGE,{"disambiguationData":[OSD([sQuery(id+"F0.wireOp",EDGE,"E24"),sQuery(id+"F0.wireOp",EDGE,"E25")])]});
            var Q83;
            Q83=makeQuery(id+"F1.opExtrude","CAP_EDGE",EDGE,{"disambiguationData":[OSD([sQuery(id+"F0.wireOp",EDGE,"E45.3")])],"isStart":false});
            var Q84;
            Q84=makeQuery(id+"F1.opExtrude","CAP_EDGE",EDGE,{"disambiguationData":[OSD([sQuery(id+"F0.wireOp",EDGE,"E32.MirrorCS")])],"isStart":true});
            var Q85;
            Q85=makeQuery(id+"F1.opExtrude","CAP_EDGE",EDGE,{"disambiguationData":[OSD([sQuery(id+"F0.wireOp",EDGE,"E43.filletArc")])],"isStart":true});
            var Q86;
            Q86=makeQuery(id+"F1.opExtrude","SWEPT_EDGE",EDGE,{"disambiguationData":[OSD([sQuery(id+"F0.wireOp",EDGE,"E22"),sQuery(id+"F0.wireOp",EDGE,"E23")])]});
            var Q87;
            Q87=makeQuery(id+"F1.opExtrude","CAP_EDGE",EDGE,{"disambiguationData":[OSD([sQuery(id+"F0.wireOp",EDGE,"E51.MirrorCS")])],"isStart":true});
            var Q88;
            Q88=makeQuery(id+"F1.opExtrude","CAP_EDGE",EDGE,{"disambiguationData":[OSD([sQuery(id+"F0.wireOp",EDGE,"E47.MirrorCS")])],"isStart":true});
            var Q89;
            Q89=makeQuery(id+"F1.opExtrude","CAP_EDGE",EDGE,{"disambiguationData":[OSD([sQuery(id+"F0.wireOp",EDGE,"E23")])],"isStart":false});
            var Q90;
            Q90=makeQuery(id+"F1.opExtrude","CAP_EDGE",EDGE,{"disambiguationData":[OSD([sQuery(id+"F0.wireOp",EDGE,"E32.MirrorCS")])],"isStart":false});
            var Q91;
            Q91=makeQuery(id+"F1.opExtrude","CAP_EDGE",EDGE,{"disambiguationData":[OSD([sQuery(id+"F0.wireOp",EDGE,"E31")])],"isStart":true});
            var Q92;
            Q92=makeQuery(id+"F1.opExtrude","CAP_EDGE",EDGE,{"disambiguationData":[OSD([sQuery(id+"F0.wireOp",EDGE,"E46")])],"isStart":true});
            var Q93;
            Q93=makeQuery(id+"F1.opExtrude","CAP_EDGE",EDGE,{"disambiguationData":[OSD([sQuery(id+"F0.wireOp",EDGE,"E48.MirrorCS")])],"isStart":true});
            var Q94;
            Q94=makeQuery(id+"F1.opExtrude","CAP_EDGE",EDGE,{"disambiguationData":[OSD([sQuery(id+"F0.wireOp",EDGE,"E30"),sQuery(id+"F0.wireOp",EDGE,"E33.MirrorCS")])],"isStart":true});
            var Q95;
            Q95=makeQuery(id+"F1.opExtrude","CAP_EDGE",EDGE,{"disambiguationData":[OSD([sQuery(id+"F0.wireOp",EDGE,"E50.MirrorCS")])],"isStart":false});
            var Q96;
            Q96=makeQuery(id+"F1.opExtrude","CAP_EDGE",EDGE,{"disambiguationData":[OSD([sQuery(id+"F0.wireOp",EDGE,"E44.top")])],"isStart":false});
            var Q97;
            Q97=makeQuery(id+"F1.opExtrude","CAP_EDGE",EDGE,{"disambiguationData":[OSD([sQuery(id+"F0.wireOp",EDGE,"E25")])],"isStart":true});
            var Q98;
            Q98=makeQuery(id+"F1.opExtrude","CAP_EDGE",EDGE,{"disambiguationData":[OSD([sQuery(id+"F0.wireOp",EDGE,"E45.3")])],"isStart":true});
            var Q99;
            Q99=makeQuery(id+"F1.opExtrude","CAP_EDGE",EDGE,{"disambiguationData":[OSD([sQuery(id+"F0.wireOp",EDGE,"E45.0")])],"isStart":true});
            var Q100;
            Q100=makeQuery(id+"F1.opExtrude","CAP_EDGE",EDGE,{"disambiguationData":[OSD([sQuery(id+"F0.wireOp",EDGE,"E27")])],"isStart":true});
            var Q101;
            Q101=makeQuery(id+"F1.opExtrude","SWEPT_EDGE",EDGE,{"disambiguationData":[OSD([sQuery(id+"F0.wireOp",EDGE,"E45.2"),sQuery(id+"F0.wireOp",EDGE,"E45.3")])]});
            var Q102;
            Q102=makeQuery(id+"F1.opExtrude","CAP_EDGE",EDGE,{"disambiguationData":[OSD([sQuery(id+"F0.wireOp",EDGE,"E22")])],"isStart":true});
            var Q103;
            Q103=makeQuery(id+"F1.opExtrude","CAP_EDGE",EDGE,{"disambiguationData":[OSD([sQuery(id+"F0.wireOp",EDGE,"E23")])],"isStart":true});
            var Q104;
            Q104=makeQuery(id+"F2.opExtrude","CAP_EDGE",EDGE,{"disambiguationData":[OSD([sQuery(id+"F0.wireOp",EDGE,"E12")])],"isStart":false});
            var Q105;
            Q105=makeQuery(id+"F2.opExtrude","CAP_EDGE",EDGE,{"disambiguationData":[OSD([sQuery(id+"F0.wireOp",EDGE,"E53")])],"isStart":false});
            var Q106;
            Q106=makeQuery(id+"F4.opChamfer","BLEND_EDGE",EDGE,{"blendedFrom":[makeQuery(id+"F2.opExtrude","CAP_EDGE",EDGE,{"disambiguationData":[OSD([sQuery(id+"F0.wireOp",EDGE,"E7")])],"isStart":false}),makeQuery(id+"F2.opExtrude","SWEPT_FACE",FACE,{"disambiguationData":[OSD([sQuery(id+"F0.wireOp",EDGE,"E8")])]})],"blendedInto":[makeQuery(id+"F2.opExtrude","SWEPT_FACE",FACE,{"disambiguationData":[OSD([sQuery(id+"F0.wireOp",EDGE,"E8")])]})]});
            var Q107;
            Q107=makeQuery(id+"F2.opExtrude","SWEPT_EDGE",EDGE,{"disambiguationData":[OSD([sQuery(id+"F0.wireOp",EDGE,"E13.top"),sQuery(id+"F0.wireOp",EDGE,"E13.left")])]});
            var Q108;
            Q108=makeQuery(id+"F2.opExtrude","CAP_EDGE",EDGE,{"disambiguationData":[OSD([sQuery(id+"F0.wireOp",EDGE,"E13.right")])],"isStart":false});
            var Q109;
            Q109=makeQuery(id+"F2.opExtrude","CAP_EDGE",EDGE,{"disambiguationData":[OSD([sQuery(id+"F0.wireOp",EDGE,"E54")])],"isStart":false});
            var Q110;
            Q110=makeQuery(id+"F2.opExtrude","CAP_EDGE",EDGE,{"disambiguationData":[OSD([sQuery(id+"F0.wireOp",EDGE,"E13.left")])],"isStart":false});
            var Q111;
            Q111=makeQuery(id+"F3.boolean.opBoolean","COPY",EDGE,{"derivedFrom":makeQuery(id+"F3.opExtrude","CAP_EDGE",EDGE,{"disambiguationData":[OSD([sQuery(id+"F0.wireOp",EDGE,"E54")])],"isStart":true})});
            var Q112;
            Q112=makeQuery(id+"F3.boolean.opBoolean","COPY",EDGE,{"derivedFrom":makeQuery(id+"F3.opExtrude","SWEPT_EDGE",EDGE,{"disambiguationData":[OSD([sQuery(id+"F0.wireOp",EDGE,"E1"),sQuery(id+"F0.wireOp",EDGE,"E16")])]})});
            var Q113;
            {var subQ0=sQuery(id+"F0.wireOp",EDGE,"E1");Q113=makeQuery(id+"F3.boolean.opBoolean","COPY",EDGE,{"derivedFrom":makeQuery(id+"F3.opExtrude","CAP_EDGE",EDGE,{"disambiguationData":[OSD([subQ0]),TDD([makeQuery(id+"F0.imprint","IMPRINT",EDGE,{"disambiguationData":[TD([[makeQuery(id+"F0.imprint","INTERSECT",VERTEX,{"derivedFrom":[subQ0,sQuery(id+"F0.wireOp",EDGE,"E14.top")]}),1.0]])],"derivedFrom":subQ0})])],"isStart":true})});}
            var Q114;
            {var subQ0=sQuery(id+"F0.wireOp",EDGE,"E54");var subQ1=sQuery(id+"F0.wireOp",EDGE,"E3");var subQ2=sQuery(id+"F0.wireOp",EDGE,"E2");Q114=makeQuery(id+"F3.boolean.opBoolean","MERGE",EDGE,{"derivedFrom":[makeQuery(id+"F2.opExtrude","SWEPT_EDGE",EDGE,{"disambiguationData":[OSD([subQ2,subQ1,subQ0])]})],"fromTools":[makeQuery(id+"F3.opExtrude","SWEPT_EDGE",EDGE,{"disambiguationData":[OSD([subQ2,subQ1,subQ0])]})]});}
            var Q115;
            Q115=makeQuery(id+"F2.opExtrude","SWEPT_EDGE",EDGE,{"disambiguationData":[OSD([sQuery(id+"F0.wireOp",EDGE,"E1"),sQuery(id+"F0.wireOp",EDGE,"E2")])]});
            var Q116;
            Q116=makeQuery(id+"F3.boolean.opBoolean","COPY",EDGE,{"derivedFrom":makeQuery(id+"F3.opExtrude","CAP_EDGE",EDGE,{"disambiguationData":[OSD([sQuery(id+"F0.wireOp",EDGE,"E54")])],"isStart":false})});
            var Q117;
            Q117=makeQuery(id+"F2.opExtrude","CAP_EDGE",EDGE,{"disambiguationData":[OSD([sQuery(id+"F0.wireOp",EDGE,"E54")])],"isStart":true});
            var Q118;
            {var subQ0=sQuery(id+"F0.wireOp",EDGE,"E52");Q118=makeQuery(id+"F3.boolean.opBoolean","COPY",EDGE,{"derivedFrom":makeQuery(id+"F3.opExtrude","CAP_EDGE",EDGE,{"disambiguationData":[OSD([subQ0]),TDD([makeQuery(id+"F0.imprint","IMPRINT",EDGE,{"disambiguationData":[TD([[makeQuery(id+"F0.imprint","INTERSECT",VERTEX,{"derivedFrom":[sQuery(id+"F0.wireOp",EDGE,"E14.bottom"),subQ0]}),1.0]])],"derivedFrom":subQ0})])],"isStart":true})});}
            var Q119;
            Q119=makeQuery(id+"F2.opExtrude","CAP_EDGE",EDGE,{"disambiguationData":[OSD([sQuery(id+"F0.wireOp",EDGE,"E2")])],"isStart":true});
            var Q120;
            Q120=makeQuery(id+"F2.opExtrude","CAP_EDGE",EDGE,{"disambiguationData":[OSD([sQuery(id+"F0.wireOp",EDGE,"E8")])],"isStart":false});
            var Q121;
            {var subQ0=sQuery(id+"F0.wireOp",EDGE,"E7");Q121=makeQuery(id+"F4.opChamfer","BLEND_EDGE",EDGE,{"blendedFrom":[makeQuery(id+"F2.opExtrude","CAP_EDGE",EDGE,{"disambiguationData":[OSD([subQ0])],"isStart":false}),makeQuery(id+"F2.opExtrude","CAP_FACE",FACE,{"disambiguationData":[OSD([sQuery(id+"F0.wireOp",EDGE,"E1"),sQuery(id+"F0.wireOp",EDGE,"E2"),sQuery(id+"F0.wireOp",EDGE,"E5"),sQuery(id+"F0.wireOp",EDGE,"E6"),subQ0,sQuery(id+"F0.wireOp",EDGE,"E8"),sQuery(id+"F0.wireOp",EDGE,"E9"),sQuery(id+"F0.wireOp",EDGE,"E12"),sQuery(id+"F0.wireOp",EDGE,"E13.bottom"),sQuery(id+"F0.wireOp",EDGE,"E13.top"),sQuery(id+"F0.wireOp",EDGE,"E13.left"),sQuery(id+"F0.wireOp",EDGE,"E13.right"),sQuery(id+"F0.wireOp",EDGE,"E53"),sQuery(id+"F0.wireOp",EDGE,"E54")])],"isStart":false})],"blendedInto":[makeQuery(id+"F2.opExtrude","CAP_FACE",FACE,{"disambiguationData":[OSD([sQuery(id+"F0.wireOp",EDGE,"E1"),sQuery(id+"F0.wireOp",EDGE,"E2"),sQuery(id+"F0.wireOp",EDGE,"E5"),sQuery(id+"F0.wireOp",EDGE,"E6"),subQ0,sQuery(id+"F0.wireOp",EDGE,"E8"),sQuery(id+"F0.wireOp",EDGE,"E9"),sQuery(id+"F0.wireOp",EDGE,"E12"),sQuery(id+"F0.wireOp",EDGE,"E13.bottom"),sQuery(id+"F0.wireOp",EDGE,"E13.top"),sQuery(id+"F0.wireOp",EDGE,"E13.left"),sQuery(id+"F0.wireOp",EDGE,"E13.right"),sQuery(id+"F0.wireOp",EDGE,"E53"),sQuery(id+"F0.wireOp",EDGE,"E54")])],"isStart":false})]});}
            var Q122;
            {var subQ0=sQuery(id+"F0.wireOp",EDGE,"E7");Q122=makeQuery(id+"F4.opChamfer","BLEND_EDGE",EDGE,{"blendedFrom":[makeQuery(id+"F2.opExtrude","CAP_EDGE",EDGE,{"disambiguationData":[OSD([subQ0])],"isStart":false}),makeQuery(id+"F2.opExtrude","SWEPT_FACE",FACE,{"disambiguationData":[OSD([subQ0])]})],"blendedInto":[makeQuery(id+"F2.opExtrude","SWEPT_FACE",FACE,{"disambiguationData":[OSD([subQ0])]})]});}
            var Q123;
            Q123=makeQuery(id+"F3.boolean.opBoolean","COPY",EDGE,{"derivedFrom":makeQuery(id+"F3.opExtrude","SWEPT_EDGE",EDGE,{"disambiguationData":[OSD([sQuery(id+"F0.wireOp",EDGE,"E3"),sQuery(id+"F0.wireOp",EDGE,"E15")])]})});
            var Q124;
            Q124=makeQuery(id+"F2.opExtrude","CAP_EDGE",EDGE,{"disambiguationData":[OSD([sQuery(id+"F0.wireOp",EDGE,"E5")])],"isStart":true});
            var Q125;
            Q125=makeQuery(id+"F3.boolean.opBoolean","COPY",EDGE,{"derivedFrom":makeQuery(id+"F3.opExtrude","CAP_EDGE",EDGE,{"disambiguationData":[OSD([sQuery(id+"F0.wireOp",EDGE,"E53")])],"isStart":true})});
            var Q126;
            Q126=makeQuery(id+"F2.opExtrude","SWEPT_EDGE",EDGE,{"disambiguationData":[OSD([sQuery(id+"F0.wireOp",EDGE,"E5"),sQuery(id+"F0.wireOp",EDGE,"E6")])]});
            var Q127;
            Q127=makeQuery(id+"F2.opExtrude","CAP_EDGE",EDGE,{"disambiguationData":[OSD([sQuery(id+"F0.wireOp",EDGE,"E1")])],"isStart":true});
            var Q128;
            {var subQ0=sQuery(id+"F0.wireOp",EDGE,"E54");var subQ1=sQuery(id+"F0.wireOp",EDGE,"E52");var subQ2=sQuery(id+"F0.wireOp",EDGE,"E14.bottom");var subQ3=sQuery(id+"F0.wireOp",EDGE,"E1");var subQ4=sQuery(id+"F0.wireOp",EDGE,"E5");var subQ5=sQuery(id+"F0.wireOp",EDGE,"E4");Q128=makeQuery(id+"F3.boolean.opBoolean","SPLIT",EDGE,{"disambiguationData":[TD([makeQuery(id+"F3.opExtrude","CAP_FACE",FACE,{"disambiguationData":[OSD([subQ3,sQuery(id+"F0.wireOp",EDGE,"E3"),subQ2,sQuery(id+"F0.wireOp",EDGE,"E15"),subQ1,subQ0])],"isStart":true})])],"derivedFrom":makeQuery(id+"F2.opExtrude","SWEPT_EDGE",EDGE,{"disambiguationData":[OSD([subQ5,subQ4,subQ1,subQ0])]})});}
            var Q129;
            {var subQ0=sQuery(id+"F0.wireOp",EDGE,"E52");Q129=makeQuery(id+"F3.boolean.opBoolean","COPY",EDGE,{"derivedFrom":makeQuery(id+"F3.opExtrude","CAP_EDGE",EDGE,{"disambiguationData":[OSD([subQ0]),TDD([makeQuery(id+"F0.imprint","IMPRINT",EDGE,{"disambiguationData":[TD([[makeQuery(id+"F0.imprint","INTERSECT",VERTEX,{"derivedFrom":[sQuery(id+"F0.wireOp",EDGE,"E14.bottom"),subQ0]}),1.0]])],"derivedFrom":subQ0})])],"isStart":false})});}
            var Q130;
            {var subQ0=sQuery(id+"F0.wireOp",EDGE,"E52");Q130=makeQuery(id+"F3.boolean.opBoolean","COPY",EDGE,{"derivedFrom":makeQuery(id+"F3.opExtrude","CAP_EDGE",EDGE,{"disambiguationData":[OSD([subQ0]),TDD([makeQuery(id+"F0.imprint","IMPRINT",EDGE,{"disambiguationData":[TD([[makeQuery(id+"F0.imprint","INTERSECT",VERTEX,{"derivedFrom":[sQuery(id+"F0.wireOp",EDGE,"E14.top"),subQ0]}),-1.0]])],"derivedFrom":subQ0})])],"isStart":false})});}
            var Q131;
            Q131=makeQuery(id+"F2.opExtrude","CAP_EDGE",EDGE,{"disambiguationData":[OSD([sQuery(id+"F0.wireOp",EDGE,"E13.right")])],"isStart":true});
            var Q132;
            Q132=makeQuery(id+"F2.opExtrude","CAP_EDGE",EDGE,{"disambiguationData":[OSD([sQuery(id+"F0.wireOp",EDGE,"E5")])],"isStart":false});
            var Q133;
            Q133=makeQuery(id+"F2.opExtrude","CAP_EDGE",EDGE,{"disambiguationData":[OSD([sQuery(id+"F0.wireOp",EDGE,"E53")])],"isStart":true});
            var Q134;
            Q134=makeQuery(id+"F2.opExtrude","CAP_EDGE",EDGE,{"disambiguationData":[OSD([sQuery(id+"F0.wireOp",EDGE,"E1")])],"isStart":false});
            var Q135;
            Q135=makeQuery(id+"F2.opExtrude","CAP_EDGE",EDGE,{"disambiguationData":[OSD([sQuery(id+"F0.wireOp",EDGE,"E2")])],"isStart":false});
            var Q136;
            Q136=makeQuery(id+"F3.boolean.opBoolean","COPY",EDGE,{"derivedFrom":makeQuery(id+"F3.opExtrude","CAP_EDGE",EDGE,{"disambiguationData":[OSD([sQuery(id+"F0.wireOp",EDGE,"E3")])],"isStart":false})});
            var Q137;
            {var subQ0=sQuery(id+"F0.wireOp",EDGE,"E1");Q137=makeQuery(id+"F3.boolean.opBoolean","COPY",EDGE,{"derivedFrom":makeQuery(id+"F3.opExtrude","CAP_EDGE",EDGE,{"disambiguationData":[OSD([subQ0]),TDD([makeQuery(id+"F0.imprint","IMPRINT",EDGE,{"disambiguationData":[TD([[makeQuery(id+"F0.imprint","INTERSECT",VERTEX,{"derivedFrom":[subQ0,sQuery(id+"F0.wireOp",EDGE,"E14.bottom")]}),-1.0]])],"derivedFrom":subQ0})])],"isStart":false})});}
            var Q138;
            Q138=makeQuery(id+"F2.opExtrude","SWEPT_EDGE",EDGE,{"disambiguationData":[OSD([sQuery(id+"F0.wireOp",EDGE,"E13.top"),sQuery(id+"F0.wireOp",EDGE,"E13.right")])]});
            var Q139;
            Q139=makeQuery(id+"F4.opChamfer","BLEND_EDGE",EDGE,{"blendedFrom":[makeQuery(id+"F2.opExtrude","CAP_EDGE",EDGE,{"disambiguationData":[OSD([sQuery(id+"F0.wireOp",EDGE,"E7")])],"isStart":true}),makeQuery(id+"F2.opExtrude","SWEPT_FACE",FACE,{"disambiguationData":[OSD([sQuery(id+"F0.wireOp",EDGE,"E6")])]})],"blendedInto":[makeQuery(id+"F2.opExtrude","SWEPT_FACE",FACE,{"disambiguationData":[OSD([sQuery(id+"F0.wireOp",EDGE,"E6")])]})]});
            var Q140;
            {var subQ0=sQuery(id+"F0.wireOp",EDGE,"E54");var subQ1=sQuery(id+"F0.wireOp",EDGE,"E3");var subQ2=sQuery(id+"F0.wireOp",EDGE,"E1");var subQ3=sQuery(id+"F0.wireOp",EDGE,"E2");Q140=makeQuery(id+"F3.boolean.opBoolean","SPLIT",EDGE,{"disambiguationData":[TD([makeQuery(id+"F3.opExtrude","CAP_FACE",FACE,{"disambiguationData":[OSD([subQ2,subQ1,sQuery(id+"F0.wireOp",EDGE,"E14.bottom"),sQuery(id+"F0.wireOp",EDGE,"E15"),sQuery(id+"F0.wireOp",EDGE,"E52"),subQ0])],"isStart":false})])],"derivedFrom":makeQuery(id+"F2.opExtrude","SWEPT_EDGE",EDGE,{"disambiguationData":[OSD([subQ3,subQ1,subQ0])]})});}
            var Q141;
            Q141=makeQuery(id+"F2.opExtrude","CAP_EDGE",EDGE,{"disambiguationData":[OSD([sQuery(id+"F0.wireOp",EDGE,"E13.top")])],"isStart":false});
            var Q142;
            Q142=makeQuery(id+"F3.boolean.opBoolean","COPY",EDGE,{"derivedFrom":makeQuery(id+"F3.opExtrude","SWEPT_EDGE",EDGE,{"disambiguationData":[OSD([sQuery(id+"F0.wireOp",EDGE,"E11"),sQuery(id+"F0.wireOp",EDGE,"E16")])]})});
            var Q143;
            Q143=makeQuery(id+"F4.opChamfer","BLEND_EDGE",EDGE,{"blendedFrom":[makeQuery(id+"F2.opExtrude","CAP_EDGE",EDGE,{"disambiguationData":[OSD([sQuery(id+"F0.wireOp",EDGE,"E7")])],"isStart":true}),makeQuery(id+"F2.opExtrude","SWEPT_FACE",FACE,{"disambiguationData":[OSD([sQuery(id+"F0.wireOp",EDGE,"E8")])]})],"blendedInto":[makeQuery(id+"F2.opExtrude","SWEPT_FACE",FACE,{"disambiguationData":[OSD([sQuery(id+"F0.wireOp",EDGE,"E8")])]})]});
            var Q144;
            Q144=makeQuery(id+"F3.boolean.opBoolean","COPY",EDGE,{"derivedFrom":makeQuery(id+"F3.opExtrude","SWEPT_EDGE",EDGE,{"disambiguationData":[OSD([sQuery(id+"F0.wireOp",EDGE,"E1"),sQuery(id+"F0.wireOp",EDGE,"E14.top")])]})});
            var Q145;
            {var subQ0=sQuery(id+"F0.wireOp",EDGE,"E1");Q145=makeQuery(id+"F3.boolean.opBoolean","COPY",EDGE,{"derivedFrom":makeQuery(id+"F3.opExtrude","CAP_EDGE",EDGE,{"disambiguationData":[OSD([subQ0]),TDD([makeQuery(id+"F0.imprint","IMPRINT",EDGE,{"disambiguationData":[TD([[makeQuery(id+"F0.imprint","INTERSECT",VERTEX,{"derivedFrom":[subQ0,sQuery(id+"F0.wireOp",EDGE,"E14.bottom")]}),-1.0]])],"derivedFrom":subQ0})])],"isStart":true})});}
            var Q146;
            Q146=makeQuery(id+"F3.boolean.opBoolean","COPY",EDGE,{"derivedFrom":makeQuery(id+"F3.opExtrude","CAP_EDGE",EDGE,{"disambiguationData":[OSD([sQuery(id+"F0.wireOp",EDGE,"E16")])],"isStart":false})});
            var Q147;
            Q147=makeQuery(id+"F2.opExtrude","CAP_EDGE",EDGE,{"disambiguationData":[OSD([sQuery(id+"F0.wireOp",EDGE,"E13.top")])],"isStart":true});
            var Q148;
            Q148=makeQuery(id+"F2.opExtrude","CAP_EDGE",EDGE,{"disambiguationData":[OSD([sQuery(id+"F0.wireOp",EDGE,"E9")])],"isStart":true});
            var Q149;
            Q149=makeQuery(id+"F2.opExtrude","SWEPT_EDGE",EDGE,{"disambiguationData":[OSD([sQuery(id+"F0.wireOp",EDGE,"E6"),sQuery(id+"F0.wireOp",EDGE,"E7")])]});
            var Q150;
            {var subQ0=sQuery(id+"F0.wireOp",EDGE,"E53");var subQ1=sQuery(id+"F0.wireOp",EDGE,"E11");var subQ2=sQuery(id+"F0.wireOp",EDGE,"E1");var subQ3=sQuery(id+"F0.wireOp",EDGE,"E12");Q150=makeQuery(id+"F3.boolean.opBoolean","SPLIT",EDGE,{"disambiguationData":[TD([makeQuery(id+"F3.opExtrude","CAP_FACE",FACE,{"disambiguationData":[OSD([subQ2,subQ1,sQuery(id+"F0.wireOp",EDGE,"E14.top"),sQuery(id+"F0.wireOp",EDGE,"E16"),sQuery(id+"F0.wireOp",EDGE,"E52"),subQ0])],"isStart":false})])],"derivedFrom":makeQuery(id+"F2.opExtrude","SWEPT_EDGE",EDGE,{"disambiguationData":[OSD([subQ1,subQ3,subQ0])]})});}
            var Q151;
            Q151=makeQuery(id+"F2.opExtrude","SWEPT_EDGE",EDGE,{"disambiguationData":[OSD([sQuery(id+"F0.wireOp",EDGE,"E13.bottom"),sQuery(id+"F0.wireOp",EDGE,"E13.left")])]});
            var Q152;
            Q152=makeQuery(id+"F3.boolean.opBoolean","COPY",EDGE,{"derivedFrom":makeQuery(id+"F3.opExtrude","SWEPT_EDGE",EDGE,{"disambiguationData":[OSD([sQuery(id+"F0.wireOp",EDGE,"E14.bottom"),sQuery(id+"F0.wireOp",EDGE,"E52")])]})});
            var Q153;
            Q153=makeQuery(id+"F2.opExtrude","SWEPT_EDGE",EDGE,{"disambiguationData":[OSD([sQuery(id+"F0.wireOp",EDGE,"E8"),sQuery(id+"F0.wireOp",EDGE,"E9")])]});
            var Q154;
            {var subQ0=sQuery(id+"F0.wireOp",EDGE,"E54");var subQ1=sQuery(id+"F0.wireOp",EDGE,"E52");var subQ2=sQuery(id+"F0.wireOp",EDGE,"E14.bottom");var subQ3=sQuery(id+"F0.wireOp",EDGE,"E1");var subQ4=sQuery(id+"F0.wireOp",EDGE,"E5");var subQ5=sQuery(id+"F0.wireOp",EDGE,"E4");Q154=makeQuery(id+"F3.boolean.opBoolean","SPLIT",EDGE,{"disambiguationData":[TD([makeQuery(id+"F3.opExtrude","CAP_FACE",FACE,{"disambiguationData":[OSD([subQ3,sQuery(id+"F0.wireOp",EDGE,"E3"),subQ2,sQuery(id+"F0.wireOp",EDGE,"E15"),subQ1,subQ0])],"isStart":false})])],"derivedFrom":makeQuery(id+"F2.opExtrude","SWEPT_EDGE",EDGE,{"disambiguationData":[OSD([subQ5,subQ4,subQ1,subQ0])]})});}
            var Q155;
            Q155=makeQuery(id+"F3.boolean.opBoolean","COPY",EDGE,{"derivedFrom":makeQuery(id+"F3.opExtrude","CAP_EDGE",EDGE,{"disambiguationData":[OSD([sQuery(id+"F0.wireOp",EDGE,"E3")])],"isStart":true})});
            var Q156;
            {var subQ0=sQuery(id+"F0.wireOp",EDGE,"E54");var subQ1=sQuery(id+"F0.wireOp",EDGE,"E3");var subQ2=sQuery(id+"F0.wireOp",EDGE,"E1");var subQ3=sQuery(id+"F0.wireOp",EDGE,"E2");Q156=makeQuery(id+"F3.boolean.opBoolean","SPLIT",EDGE,{"disambiguationData":[TD([makeQuery(id+"F3.opExtrude","CAP_FACE",FACE,{"disambiguationData":[OSD([subQ2,subQ1,sQuery(id+"F0.wireOp",EDGE,"E14.bottom"),sQuery(id+"F0.wireOp",EDGE,"E15"),sQuery(id+"F0.wireOp",EDGE,"E52"),subQ0])],"isStart":true})])],"derivedFrom":makeQuery(id+"F2.opExtrude","SWEPT_EDGE",EDGE,{"disambiguationData":[OSD([subQ3,subQ1,subQ0])]})});}
            var Q157;
            Q157=makeQuery(id+"F2.opExtrude","SWEPT_EDGE",EDGE,{"disambiguationData":[OSD([sQuery(id+"F0.wireOp",EDGE,"E1"),sQuery(id+"F0.wireOp",EDGE,"E12")])]});
            var Q158;
            Q158=makeQuery(id+"F3.boolean.opBoolean","COPY",EDGE,{"derivedFrom":makeQuery(id+"F3.opExtrude","CAP_EDGE",EDGE,{"disambiguationData":[OSD([sQuery(id+"F0.wireOp",EDGE,"E16")])],"isStart":true})});
            var Q159;
            Q159=makeQuery(id+"F2.opExtrude","CAP_EDGE",EDGE,{"disambiguationData":[OSD([sQuery(id+"F0.wireOp",EDGE,"E13.bottom")])],"isStart":true});
            var Q160;
            Q160=makeQuery(id+"F3.boolean.opBoolean","COPY",EDGE,{"derivedFrom":makeQuery(id+"F3.opExtrude","CAP_EDGE",EDGE,{"disambiguationData":[OSD([sQuery(id+"F0.wireOp",EDGE,"E53")])],"isStart":false})});
            var Q161;
            {var subQ0=sQuery(id+"F0.wireOp",EDGE,"E1");Q161=makeQuery(id+"F3.boolean.opBoolean","COPY",EDGE,{"derivedFrom":makeQuery(id+"F3.opExtrude","CAP_EDGE",EDGE,{"disambiguationData":[OSD([subQ0]),TDD([makeQuery(id+"F0.imprint","IMPRINT",EDGE,{"disambiguationData":[TD([[makeQuery(id+"F0.imprint","INTERSECT",VERTEX,{"derivedFrom":[subQ0,sQuery(id+"F0.wireOp",EDGE,"E14.top")]}),1.0]])],"derivedFrom":subQ0})])],"isStart":false})});}
            var Q162;
            Q162=makeQuery(id+"F2.opExtrude","CAP_EDGE",EDGE,{"disambiguationData":[OSD([sQuery(id+"F0.wireOp",EDGE,"E13.bottom")])],"isStart":false});
            var Q163;
            Q163=makeQuery(id+"F2.opExtrude","SWEPT_EDGE",EDGE,{"disambiguationData":[OSD([sQuery(id+"F0.wireOp",EDGE,"E13.bottom"),sQuery(id+"F0.wireOp",EDGE,"E13.right")])]});
            var Q164;
            Q164=makeQuery(id+"F3.boolean.opBoolean","COPY",EDGE,{"derivedFrom":makeQuery(id+"F3.opExtrude","SWEPT_EDGE",EDGE,{"disambiguationData":[OSD([sQuery(id+"F0.wireOp",EDGE,"E1"),sQuery(id+"F0.wireOp",EDGE,"E14.bottom")])]})});
            var Q165;
            Q165=makeQuery(id+"F2.opExtrude","CAP_EDGE",EDGE,{"disambiguationData":[OSD([sQuery(id+"F0.wireOp",EDGE,"E9")])],"isStart":false});
            var Q166;
            Q166=makeQuery(id+"F3.boolean.opBoolean","COPY",EDGE,{"derivedFrom":makeQuery(id+"F3.opExtrude","SWEPT_EDGE",EDGE,{"disambiguationData":[OSD([sQuery(id+"F0.wireOp",EDGE,"E1"),sQuery(id+"F0.wireOp",EDGE,"E15")])]})});
            var Q167;
            Q167=makeQuery(id+"F2.opExtrude","SWEPT_EDGE",EDGE,{"disambiguationData":[OSD([sQuery(id+"F0.wireOp",EDGE,"E7"),sQuery(id+"F0.wireOp",EDGE,"E8")])]});
            var Q168;
            {var subQ0=sQuery(id+"F0.wireOp",EDGE,"E7");Q168=makeQuery(id+"F4.opChamfer","BLEND_EDGE",EDGE,{"blendedFrom":[makeQuery(id+"F2.opExtrude","CAP_EDGE",EDGE,{"disambiguationData":[OSD([subQ0])],"isStart":true}),makeQuery(id+"F2.opExtrude","SWEPT_FACE",FACE,{"disambiguationData":[OSD([subQ0])]})],"blendedInto":[makeQuery(id+"F2.opExtrude","SWEPT_FACE",FACE,{"disambiguationData":[OSD([subQ0])]})]});}
            var Q169;
            Q169=makeQuery(id+"F2.opExtrude","CAP_EDGE",EDGE,{"disambiguationData":[OSD([sQuery(id+"F0.wireOp",EDGE,"E6")])],"isStart":true});
            var Q170;
            {var subQ0=sQuery(id+"F0.wireOp",EDGE,"E7");Q170=makeQuery(id+"F4.opChamfer","BLEND_EDGE",EDGE,{"blendedFrom":[makeQuery(id+"F2.opExtrude","CAP_EDGE",EDGE,{"disambiguationData":[OSD([subQ0])],"isStart":true}),makeQuery(id+"F2.opExtrude","CAP_FACE",FACE,{"disambiguationData":[OSD([sQuery(id+"F0.wireOp",EDGE,"E1"),sQuery(id+"F0.wireOp",EDGE,"E2"),sQuery(id+"F0.wireOp",EDGE,"E5"),sQuery(id+"F0.wireOp",EDGE,"E6"),subQ0,sQuery(id+"F0.wireOp",EDGE,"E8"),sQuery(id+"F0.wireOp",EDGE,"E9"),sQuery(id+"F0.wireOp",EDGE,"E12"),sQuery(id+"F0.wireOp",EDGE,"E13.bottom"),sQuery(id+"F0.wireOp",EDGE,"E13.top"),sQuery(id+"F0.wireOp",EDGE,"E13.left"),sQuery(id+"F0.wireOp",EDGE,"E13.right"),sQuery(id+"F0.wireOp",EDGE,"E53"),sQuery(id+"F0.wireOp",EDGE,"E54")])],"isStart":true})],"blendedInto":[makeQuery(id+"F2.opExtrude","CAP_FACE",FACE,{"disambiguationData":[OSD([sQuery(id+"F0.wireOp",EDGE,"E1"),sQuery(id+"F0.wireOp",EDGE,"E2"),sQuery(id+"F0.wireOp",EDGE,"E5"),sQuery(id+"F0.wireOp",EDGE,"E6"),subQ0,sQuery(id+"F0.wireOp",EDGE,"E8"),sQuery(id+"F0.wireOp",EDGE,"E9"),sQuery(id+"F0.wireOp",EDGE,"E12"),sQuery(id+"F0.wireOp",EDGE,"E13.bottom"),sQuery(id+"F0.wireOp",EDGE,"E13.top"),sQuery(id+"F0.wireOp",EDGE,"E13.left"),sQuery(id+"F0.wireOp",EDGE,"E13.right"),sQuery(id+"F0.wireOp",EDGE,"E53"),sQuery(id+"F0.wireOp",EDGE,"E54")])],"isStart":true})]});}
            var Q171;
            Q171=makeQuery(id+"F2.opExtrude","CAP_EDGE",EDGE,{"disambiguationData":[OSD([sQuery(id+"F0.wireOp",EDGE,"E6")])],"isStart":false});
            var Q172;
            Q172=makeQuery(id+"F4.opChamfer","BLEND_EDGE",EDGE,{"blendedFrom":[makeQuery(id+"F2.opExtrude","CAP_EDGE",EDGE,{"disambiguationData":[OSD([sQuery(id+"F0.wireOp",EDGE,"E7")])],"isStart":false}),makeQuery(id+"F2.opExtrude","SWEPT_FACE",FACE,{"disambiguationData":[OSD([sQuery(id+"F0.wireOp",EDGE,"E6")])]})],"blendedInto":[makeQuery(id+"F2.opExtrude","SWEPT_FACE",FACE,{"disambiguationData":[OSD([sQuery(id+"F0.wireOp",EDGE,"E6")])]})]});
            var Q173;
            Q173=makeQuery(id+"F2.opExtrude","CAP_EDGE",EDGE,{"disambiguationData":[OSD([sQuery(id+"F0.wireOp",EDGE,"E8")])],"isStart":true});
            var Q174;
            Q174=makeQuery(id+"F2.opExtrude","CAP_EDGE",EDGE,{"disambiguationData":[OSD([sQuery(id+"F0.wireOp",EDGE,"E13.left")])],"isStart":true});
            var Q175;
            {var subQ0=sQuery(id+"F0.wireOp",EDGE,"E53");var subQ1=sQuery(id+"F0.wireOp",EDGE,"E52");var subQ2=sQuery(id+"F0.wireOp",EDGE,"E14.top");var subQ3=sQuery(id+"F0.wireOp",EDGE,"E1");var subQ4=sQuery(id+"F0.wireOp",EDGE,"E9");var subQ5=sQuery(id+"F0.wireOp",EDGE,"E10");Q175=makeQuery(id+"F3.boolean.opBoolean","SPLIT",EDGE,{"disambiguationData":[TD([makeQuery(id+"F3.opExtrude","CAP_FACE",FACE,{"disambiguationData":[OSD([subQ3,sQuery(id+"F0.wireOp",EDGE,"E11"),subQ2,sQuery(id+"F0.wireOp",EDGE,"E16"),subQ1,subQ0])],"isStart":true})])],"derivedFrom":makeQuery(id+"F2.opExtrude","SWEPT_EDGE",EDGE,{"disambiguationData":[OSD([subQ4,subQ5,subQ1,subQ0])]})});}
            var Q176;
            Q176=makeQuery(id+"F3.boolean.opBoolean","COPY",EDGE,{"derivedFrom":makeQuery(id+"F3.opExtrude","CAP_EDGE",EDGE,{"disambiguationData":[OSD([sQuery(id+"F0.wireOp",EDGE,"E14.bottom")])],"isStart":true})});
            var Q177;
            Q177=makeQuery(id+"F3.boolean.opBoolean","COPY",EDGE,{"derivedFrom":makeQuery(id+"F3.opExtrude","CAP_EDGE",EDGE,{"disambiguationData":[OSD([sQuery(id+"F0.wireOp",EDGE,"E11")])],"isStart":false})});
            var Q178;
            {var subQ0=sQuery(id+"F0.wireOp",EDGE,"E52");Q178=makeQuery(id+"F3.boolean.opBoolean","COPY",EDGE,{"derivedFrom":makeQuery(id+"F3.opExtrude","CAP_EDGE",EDGE,{"disambiguationData":[OSD([subQ0]),TDD([makeQuery(id+"F0.imprint","IMPRINT",EDGE,{"disambiguationData":[TD([[makeQuery(id+"F0.imprint","INTERSECT",VERTEX,{"derivedFrom":[sQuery(id+"F0.wireOp",EDGE,"E14.top"),subQ0]}),-1.0]])],"derivedFrom":subQ0})])],"isStart":true})});}
            var Q179;
            Q179=makeQuery(id+"F3.boolean.opBoolean","COPY",EDGE,{"derivedFrom":makeQuery(id+"F3.opExtrude","CAP_EDGE",EDGE,{"disambiguationData":[OSD([sQuery(id+"F0.wireOp",EDGE,"E14.bottom")])],"isStart":false})});
            var Q180;
            Q180=makeQuery(id+"F3.boolean.opBoolean","COPY",EDGE,{"derivedFrom":makeQuery(id+"F3.opExtrude","CAP_EDGE",EDGE,{"disambiguationData":[OSD([sQuery(id+"F0.wireOp",EDGE,"E14.top")])],"isStart":false})});
            var Q181;
            Q181=makeQuery(id+"F3.boolean.opBoolean","COPY",EDGE,{"derivedFrom":makeQuery(id+"F3.opExtrude","CAP_EDGE",EDGE,{"disambiguationData":[OSD([sQuery(id+"F0.wireOp",EDGE,"E11")])],"isStart":true})});
            var Q182;
            Q182=makeQuery(id+"F2.opExtrude","CAP_EDGE",EDGE,{"disambiguationData":[OSD([sQuery(id+"F0.wireOp",EDGE,"E12")])],"isStart":true});
            var Q183;
            Q183=makeQuery(id+"F3.boolean.opBoolean","COPY",EDGE,{"derivedFrom":makeQuery(id+"F3.opExtrude","SWEPT_EDGE",EDGE,{"disambiguationData":[OSD([sQuery(id+"F0.wireOp",EDGE,"E14.top"),sQuery(id+"F0.wireOp",EDGE,"E52")])]})});
            var Q184;
            {var subQ0=sQuery(id+"F0.wireOp",EDGE,"E53");var subQ1=sQuery(id+"F0.wireOp",EDGE,"E52");var subQ2=sQuery(id+"F0.wireOp",EDGE,"E14.top");var subQ3=sQuery(id+"F0.wireOp",EDGE,"E1");var subQ4=sQuery(id+"F0.wireOp",EDGE,"E9");var subQ5=sQuery(id+"F0.wireOp",EDGE,"E10");Q184=makeQuery(id+"F3.boolean.opBoolean","SPLIT",EDGE,{"disambiguationData":[TD([makeQuery(id+"F3.opExtrude","CAP_FACE",FACE,{"disambiguationData":[OSD([subQ3,sQuery(id+"F0.wireOp",EDGE,"E11"),subQ2,sQuery(id+"F0.wireOp",EDGE,"E16"),subQ1,subQ0])],"isStart":false})])],"derivedFrom":makeQuery(id+"F2.opExtrude","SWEPT_EDGE",EDGE,{"disambiguationData":[OSD([subQ4,subQ5,subQ1,subQ0])]})});}
            var Q185;
            {var subQ0=sQuery(id+"F0.wireOp",EDGE,"E53");var subQ1=sQuery(id+"F0.wireOp",EDGE,"E12");var subQ2=sQuery(id+"F0.wireOp",EDGE,"E11");Q185=makeQuery(id+"F3.boolean.opBoolean","MERGE",EDGE,{"derivedFrom":[makeQuery(id+"F2.opExtrude","SWEPT_EDGE",EDGE,{"disambiguationData":[OSD([subQ2,subQ1,subQ0])]})],"fromTools":[makeQuery(id+"F3.opExtrude","SWEPT_EDGE",EDGE,{"disambiguationData":[OSD([subQ2,subQ1,subQ0])]})]});}
            var Q186;
            Q186=makeQuery(id+"F3.boolean.opBoolean","COPY",EDGE,{"derivedFrom":makeQuery(id+"F3.opExtrude","CAP_EDGE",EDGE,{"disambiguationData":[OSD([sQuery(id+"F0.wireOp",EDGE,"E15")])],"isStart":true})});
            var Q187;
            Q187=makeQuery(id+"F3.boolean.opBoolean","COPY",EDGE,{"derivedFrom":makeQuery(id+"F3.opExtrude","CAP_EDGE",EDGE,{"disambiguationData":[OSD([sQuery(id+"F0.wireOp",EDGE,"E14.top")])],"isStart":true})});
            var Q188;
            Q188=makeQuery(id+"F3.boolean.opBoolean","COPY",EDGE,{"derivedFrom":makeQuery(id+"F3.opExtrude","CAP_EDGE",EDGE,{"disambiguationData":[OSD([sQuery(id+"F0.wireOp",EDGE,"E15")])],"isStart":false})});
            var Q189;
            {var subQ0=sQuery(id+"F0.wireOp",EDGE,"E53");var subQ1=sQuery(id+"F0.wireOp",EDGE,"E11");var subQ2=sQuery(id+"F0.wireOp",EDGE,"E1");var subQ3=sQuery(id+"F0.wireOp",EDGE,"E12");Q189=makeQuery(id+"F3.boolean.opBoolean","SPLIT",EDGE,{"disambiguationData":[TD([makeQuery(id+"F3.opExtrude","CAP_FACE",FACE,{"disambiguationData":[OSD([subQ2,subQ1,sQuery(id+"F0.wireOp",EDGE,"E14.top"),sQuery(id+"F0.wireOp",EDGE,"E16"),sQuery(id+"F0.wireOp",EDGE,"E52"),subQ0])],"isStart":true})])],"derivedFrom":makeQuery(id+"F2.opExtrude","SWEPT_EDGE",EDGE,{"disambiguationData":[OSD([subQ1,subQ3,subQ0])]})});}
            fillet(context, id + "F5", {"entities" : qUnion([Q0, Q1, Q2, Q3, Q4, Q5, Q6, Q7, Q8, Q9, Q10, Q11, Q12, Q13, Q14, Q15, Q16, Q17, Q18, Q19, Q20, Q21, Q22, Q23, Q24, Q25, Q26, Q27, Q28, Q29, Q30, Q31, Q32, Q33, Q34, Q35, Q36, Q37, Q38, Q39, Q40, Q41, Q42, Q43, Q44, Q45, Q46, Q47, Q48, Q49, Q50, Q51, Q52, Q53, Q54, Q55, Q56, Q57, Q58, Q59, Q60, Q61, Q62, Q63, Q64, Q65, Q66, Q67, Q68, Q69, Q70, Q71, Q72, Q73, Q74, Q75, Q76, Q77, Q78, Q79, Q80, Q81, Q82, Q83, Q84, Q85, Q86, Q87, Q88, Q89, Q90, Q91, Q92, Q93, Q94, Q95, Q96, Q97, Q98, Q99, Q100, Q101, Q102, Q103, Q104, Q105, Q106, Q107, Q108, Q109, Q110, Q111, Q112, Q113, Q114, Q115, Q116, Q117, Q118, Q119, Q120, Q121, Q122, Q123, Q124, Q125, Q126, Q127, Q128, Q129, Q130, Q131, Q132, Q133, Q134, Q135, Q136, Q137, Q138, Q139, Q140, Q141, Q142, Q143, Q144, Q145, Q146, Q147, Q148, Q149, Q150, Q151, Q152, Q153, Q154, Q155, Q156, Q157, Q158, Q159, Q160, Q161, Q162, Q163, Q164, Q165, Q166, Q167, Q168, Q169, Q170, Q171, Q172, Q173, Q174, Q175, Q176, Q177, Q178, Q179, Q180, Q181, Q182, Q183, Q184, Q185, Q186, Q187, Q188, Q189]), "radius" : .5 * mm, "tangentPropagation" : true, "allowEdgeOverflow" : false});
        }
        {
            var Q0;
            Q0=qCreatedBy(makeId("Top.planeOp"),FACE);
            var sketch = newSketch(context, id + "F6", { "sketchPlane" : qUnion([Q0])});
            skText(sketch, "E55", { "text": "EMC", "fontName": "NotoSans-Regular.ttf"});
            skLineSegment(sketch, "E56.0", {"start": v(-38, 16) * mm, "end": v(-10, 16) * mm, "construction": true});
            skLineSegment(sketch, "E57.0", {"start": v(-50, 15) * mm, "end": v(-10, 15) * mm, "construction": true});
            skLineSegment(sketch, "E58", {"start": v(-24, 16) * mm, "end": v(-24, 15) * mm, "construction": true});
            const initialGuessF6  = {"E55": [-0.034, 0.01162, 1, 0, 0.00676]};
            skSetInitialGuess(sketch, initialGuessF6);
            skSolve(sketch);
        }
        {
            var Q0;
            Q0 = qSketchRegion(id + "F6", true);
            extrude(context, id + "F7", {"entities" : qUnion([Q0]), "operationType" : NewBodyOperationType.REMOVE, "depth" : 1.5 * mm, "offsetDistance" : 25 * mm});
        }
    });
